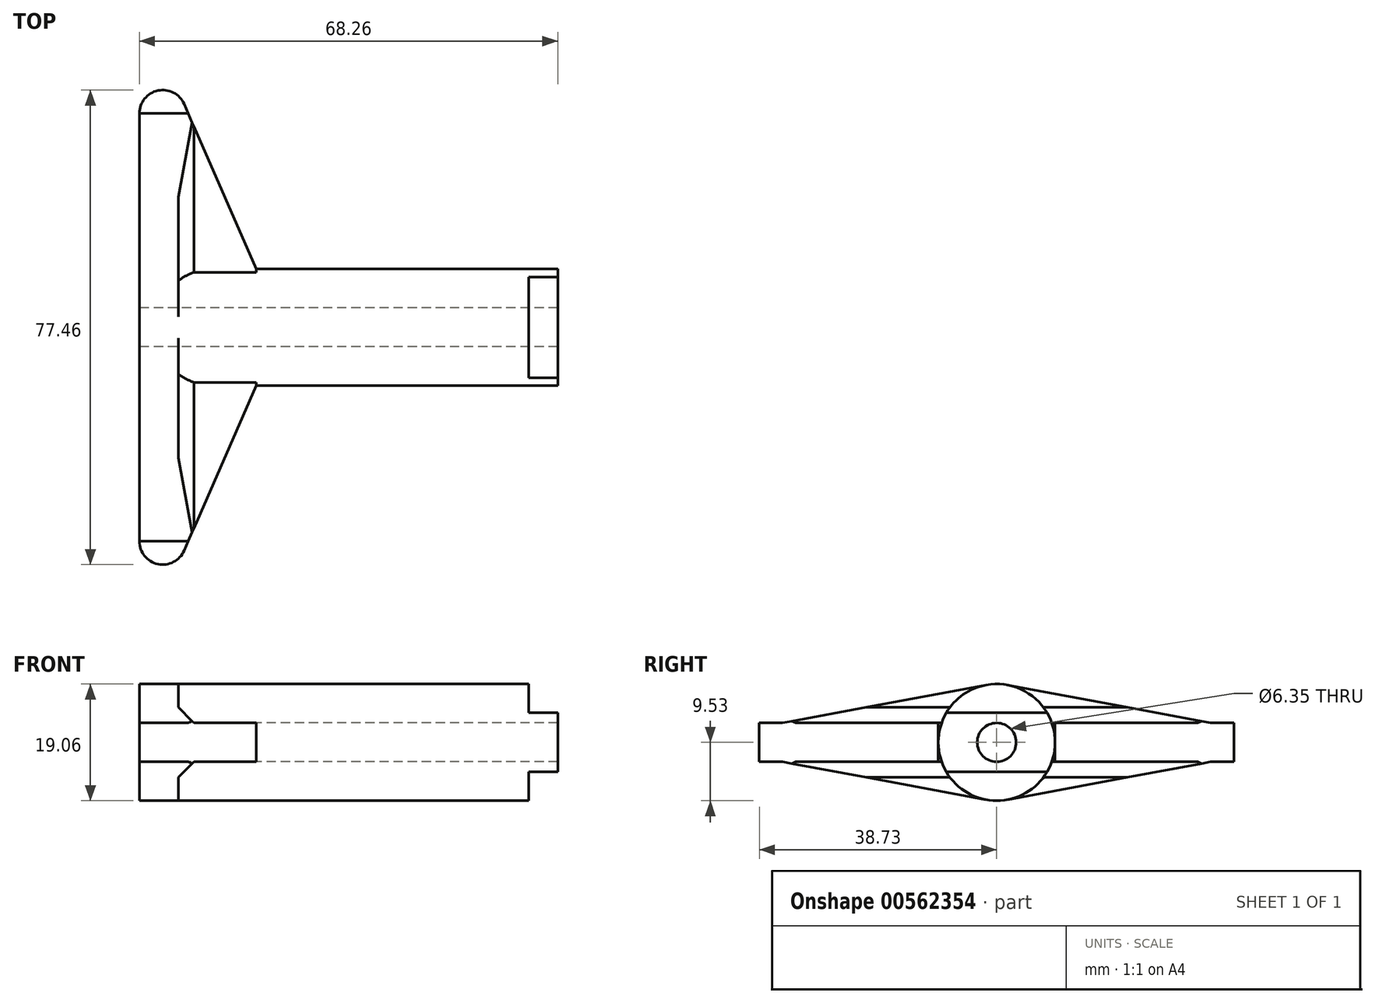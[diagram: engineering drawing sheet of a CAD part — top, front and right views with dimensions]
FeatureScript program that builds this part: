
annotation { "Feature Type Name" : "Feature", "Feature Type Description" : "" }
export const myFeature = defineFeature(function(context is Context, id is Id, definition is map)
    precondition{}
    {
        {
            var Q0;
            Q0=qCreatedBy(makeId("Right.planeOp"),FACE);
            var sketch = newSketch(context, id + "F0", { "sketchPlane" : qUnion([Q0])});
            skCircle(sketch, "E0", {"center": v(0, 0) * mm, "radius": 9.53 * mm});
            skCircle(sketch, "E1", {"center": v(0, 0) * mm, "radius": 3.18 * mm});
            skLineSegment(sketch, "E2", {"start": v(-15.88, 4.83) * mm, "end": v(24.18, 4.83) * mm});
            skLineSegment(sketch, "E3", {"start": v(26.07, -4.83) * mm, "end": v(-16.45, -4.83) * mm});
            skSolve(sketch);
        }
        {
            var Q0;
            Q0=makeQuery(id+"F0.imprint","IMPRINT",FACE,{"disambiguationData":[TD([[makeQuery(id+"F0.imprint","IMPRINT",EDGE,{"derivedFrom":sQuery(id+"F0.wireOp",EDGE,"E1")}),-1.0]])]});
            extrude(context, id + "F1", {"entities" : qUnion([Q0]), "depth" : 4.76 * mm, "offsetDistance" : 25.4 * mm});
        }
        {
            var Q0;
            Q0=makeQuery(id+"F1.opExtrude","CAP_FACE",FACE,{"disambiguationData":[OSD([sQuery(id+"F0.wireOp",EDGE,"E0"),sQuery(id+"F0.wireOp",EDGE,"E1"),sQuery(id+"F0.wireOp",EDGE,"E2"),sQuery(id+"F0.wireOp",EDGE,"E3")])],"isStart":true});
            var sketch = newSketch(context, id + "F2", { "sketchPlane" : qUnion([Q0])});
            skArc(sketch, "E4.0", {"start": v(-8.21, -4.83) * mm, "mid": v(-9.53, 0) * mm, "end": v(-8.21, 4.83) * mm});
            skCircle(sketch, "E5.0", {"center": v(0, 0) * mm, "radius": 3.18 * mm});
            skCircle(sketch, "E6", {"center": v(0, 0) * mm, "radius": 9.53 * mm});
            skSolve(sketch);
        }
        {
            var Q0;
            Q0 = qSketchRegion(id + "F2", true);
            extrude(context, id + "F3", {"entities" : qUnion([Q0]), "operationType" : NewBodyOperationType.ADD, "depth" : 63.5 * mm, "offsetDistance" : 25.4 * mm});
        }
        {
            var Q0;
            Q0=qCreatedBy(makeId("Top.planeOp"),FACE);
            var sketch = newSketch(context, id + "F4", { "sketchPlane" : qUnion([Q0])});
            skLineSegment(sketch, "E7.0", {"start": v(-63.5, -9.53) * mm, "end": v(-63.5, 9.52) * mm});
            skLineSegment(sketch, "E8", {"start": v(-63.5, 9.52) * mm, "end": v(-63.5, 34.92) * mm});
            skArc(sketch, "E9", {"start": v(-56.2, 36.45) * mm, "mid": v(-60.47, 38.65) * mm, "end": v(-63.5, 34.92) * mm});
            skLineSegment(sketch, "E10", {"start": v(-56.2, 36.45) * mm, "end": v(-44.45, 9.52) * mm});
            skLineSegment(sketch, "E11", {"start": v(-44.45, 9.52) * mm, "end": v(-44.45, -9.53) * mm});
            skLineSegment(sketch, "E12", {"start": v(-44.45, -9.52) * mm, "end": v(-56.2, -36.45) * mm});
            skArc(sketch, "E13", {"start": v(-63.5, -34.93) * mm, "mid": v(-60.47, -38.65) * mm, "end": v(-56.2, -36.45) * mm});
            skLineSegment(sketch, "E14", {"start": v(-63.5, -34.93) * mm, "end": v(-63.5, -9.53) * mm});
            skLineSegment(sketch, "E15", {"start": v(-63.5, -9.52) * mm, "end": v(-44.45, -9.52) * mm});
            skLineSegment(sketch, "E16", {"start": v(-63.5, 9.53) * mm, "end": v(-44.45, 9.53) * mm});
            skSolve(sketch);
        }
        {
            var Q0;
            Q0 = qSketchRegion(id + "F4", true);
            extrude(context, id + "F5", {"entities" : qUnion([Q0]), "operationType" : NewBodyOperationType.ADD, "endBound" : BoundingType.SYMMETRIC, "depth" : 6.35 * mm, "offsetDistance" : 25.4 * mm});
        }
        {
            var Q0;
            Q0=makeQuery(id+"F5.boolean.opBoolean","MERGE",FACE,{"derivedFrom":[makeQuery(id+"F3.opExtrude","CAP_FACE",FACE,{"disambiguationData":[OSD([sQuery(id+"F2.wireOp",EDGE,"E5.0"),sQuery(id+"F2.wireOp",EDGE,"E6")])],"isStart":false}),makeQuery(id+"F5.opExtrude","SWEPT_FACE",FACE,{"disambiguationData":[OSD([sQuery(id+"F4.wireOp",EDGE,"E7.0"),sQuery(id+"F4.wireOp",EDGE,"E8"),sQuery(id+"F4.wireOp",EDGE,"E14")])]})]});
            var sketch = newSketch(context, id + "F6", { "sketchPlane" : qUnion([Q0])});
            skLineSegment(sketch, "E17", {"start": v(-34.92, 3.18) * mm, "end": v(0, 9.69) * mm});
            skPoint(sketch, "E17.endSnap0", {"position": v(0, 9.53) * mm});
            skLineSegment(sketch, "E18", {"start": v(0, 9.69) * mm, "end": v(34.93, 3.18) * mm});
            skLineSegment(sketch, "E19", {"start": v(34.93, 3.18) * mm, "end": v(34.93, -3.18) * mm});
            skLineSegment(sketch, "E20", {"start": v(34.93, -3.17) * mm, "end": v(0, -9.69) * mm});
            skLineSegment(sketch, "E21", {"start": v(0, -9.69) * mm, "end": v(-34.92, -3.18) * mm});
            skLineSegment(sketch, "E22", {"start": v(-34.92, -3.17) * mm, "end": v(-34.92, 3.17) * mm});
            skSolve(sketch);
        }
        {
            var Q0;
            Q0 = qSketchRegion(id + "F6", true);
            var Q1;
            {var subQ0=sQuery(id+"F6.wireOp",EDGE,"E21");Q1=makeQuery(id+"F6.imprint","IMPRINT",FACE,{"disambiguationData":[TD([[makeQuery(id+"F6.imprint","IMPRINT",EDGE,{"derivedFrom":subQ0}),-1.0]])]});}
            var Q2;
            {var subQ9=sQuery(id+"F4.wireOp",EDGE,"E14");var subQ10=sQuery(id+"F4.wireOp",EDGE,"E9");var subQ11=sQuery(id+"F4.wireOp",EDGE,"E8");var subQ12=sQuery(id+"F4.wireOp",EDGE,"E7.0");var subQ15=makeQuery(id+"F5.boolean.opBoolean","SPLIT",EDGE,{"disambiguationData":[TD([makeQuery(id+"F5.opExtrude","SWEPT_FACE",FACE,{"disambiguationData":[OSD([subQ10])]})])],"derivedFrom":makeQuery(id+"F5.opExtrude","CAP_EDGE",EDGE,{"disambiguationData":[OSD([subQ12,subQ11,subQ9])],"isStart":false})});Q2=makeQuery(id+"F6.imprint","IMPRINT",FACE,{"disambiguationData":[TD([[makeQuery(id+"F6.imprint","IMPRINT",EDGE,{"derivedFrom":subQ15}),-1.0]])]});}
            var Q3;
            {var subQ0=sQuery(id+"F6.wireOp",EDGE,"E18");Q3=makeQuery(id+"F6.imprint","IMPRINT",FACE,{"disambiguationData":[TD([[makeQuery(id+"F6.imprint","IMPRINT",EDGE,{"derivedFrom":subQ0}),-1.0]])]});}
            var Q4;
            {var subQ9=sQuery(id+"F4.wireOp",EDGE,"E14");var subQ10=sQuery(id+"F4.wireOp",EDGE,"E13");var subQ11=sQuery(id+"F4.wireOp",EDGE,"E8");var subQ12=sQuery(id+"F4.wireOp",EDGE,"E7.0");var subQ15=makeQuery(id+"F5.boolean.opBoolean","SPLIT",EDGE,{"disambiguationData":[TD([makeQuery(id+"F5.opExtrude","SWEPT_FACE",FACE,{"disambiguationData":[OSD([subQ10])]})])],"derivedFrom":makeQuery(id+"F5.opExtrude","CAP_EDGE",EDGE,{"disambiguationData":[OSD([subQ12,subQ11,subQ9])],"isStart":true})});Q4=makeQuery(id+"F6.imprint","IMPRINT",FACE,{"disambiguationData":[TD([[makeQuery(id+"F6.imprint","IMPRINT",EDGE,{"derivedFrom":subQ15}),1.0]])]});}
            var Q5;
            Q5=makeQuery(id+"F6.imprint","IMPRINT",FACE,{"disambiguationData":[TD([[makeQuery(id+"F6.imprint","IMPRINT",EDGE,{"derivedFrom":sQuery(id+"F6.wireOp",EDGE,"E19")}),-1.0]])]});
            extrude(context, id + "F7", {"entities" : qUnion([Q0, Q1, Q2, Q3, Q4, Q5]), "operationType" : NewBodyOperationType.ADD, "oppositeDirection" : true, "depth" : 6.35 * mm, "offsetDistance" : 25.4 * mm});
        }
        {
            var Q0;
            {var subQ0=sQuery(id+"F2.wireOp",EDGE,"E6");var subQ4=sQuery(id+"F4.wireOp",EDGE,"E11");var subQ5=sQuery(id+"F4.wireOp",EDGE,"E14");var subQ6=sQuery(id+"F4.wireOp",EDGE,"E8");var subQ7=sQuery(id+"F4.wireOp",EDGE,"E7.0");var subQ8=sQuery(id+"F4.wireOp",EDGE,"E9");var subQ9=sQuery(id+"F4.wireOp",EDGE,"E10");Q0=makeQuery(id+"F7.boolean.opBoolean","INTERSECT",EDGE,{"derivedFrom":[makeQuery(id+"F5.boolean.opBoolean","SPLIT",FACE,{"disambiguationData":[TD([makeQuery(id+"F5.opExtrude","SWEPT_FACE",FACE,{"disambiguationData":[OSD([subQ8])]})])],"derivedFrom":makeQuery(id+"F5.opExtrude","CAP_FACE",FACE,{"disambiguationData":[OSD([subQ7,subQ6,subQ8,subQ9,subQ4,sQuery(id+"F4.wireOp",EDGE,"E12"),sQuery(id+"F4.wireOp",EDGE,"E13"),subQ5])],"isStart":false})}),makeQuery(id+"F7.opExtrude","CAP_FACE",FACE,{"disambiguationData":[OSD([subQ0,sQuery(id+"F6.wireOp",EDGE,"E17"),sQuery(id+"F6.wireOp",EDGE,"E18"),sQuery(id+"F6.wireOp",EDGE,"E19"),sQuery(id+"F6.wireOp",EDGE,"E20"),sQuery(id+"F6.wireOp",EDGE,"E21"),sQuery(id+"F6.wireOp",EDGE,"E22")])],"isStart":false})]});}
            var Q1;
            {var subQ0=sQuery(id+"F2.wireOp",EDGE,"E6");var subQ4=sQuery(id+"F4.wireOp",EDGE,"E11");var subQ5=sQuery(id+"F4.wireOp",EDGE,"E14");var subQ6=sQuery(id+"F4.wireOp",EDGE,"E8");var subQ7=sQuery(id+"F4.wireOp",EDGE,"E7.0");var subQ8=sQuery(id+"F4.wireOp",EDGE,"E9");var subQ9=sQuery(id+"F4.wireOp",EDGE,"E10");Q1=makeQuery(id+"F7.boolean.opBoolean","INTERSECT",EDGE,{"derivedFrom":[makeQuery(id+"F5.boolean.opBoolean","SPLIT",FACE,{"disambiguationData":[TD([makeQuery(id+"F5.opExtrude","SWEPT_FACE",FACE,{"disambiguationData":[OSD([subQ8])]})])],"derivedFrom":makeQuery(id+"F5.opExtrude","CAP_FACE",FACE,{"disambiguationData":[OSD([subQ7,subQ6,subQ8,subQ9,subQ4,sQuery(id+"F4.wireOp",EDGE,"E12"),sQuery(id+"F4.wireOp",EDGE,"E13"),subQ5])],"isStart":true})}),makeQuery(id+"F7.opExtrude","CAP_FACE",FACE,{"disambiguationData":[OSD([subQ0,sQuery(id+"F6.wireOp",EDGE,"E17"),sQuery(id+"F6.wireOp",EDGE,"E18"),sQuery(id+"F6.wireOp",EDGE,"E19"),sQuery(id+"F6.wireOp",EDGE,"E20"),sQuery(id+"F6.wireOp",EDGE,"E21"),sQuery(id+"F6.wireOp",EDGE,"E22")])],"isStart":false})]});}
            var Q2;
            {var subQ0=sQuery(id+"F2.wireOp",EDGE,"E6");var subQ4=sQuery(id+"F4.wireOp",EDGE,"E11");var subQ5=sQuery(id+"F4.wireOp",EDGE,"E14");var subQ6=sQuery(id+"F4.wireOp",EDGE,"E8");var subQ7=sQuery(id+"F4.wireOp",EDGE,"E7.0");var subQ8=sQuery(id+"F4.wireOp",EDGE,"E12");var subQ9=sQuery(id+"F4.wireOp",EDGE,"E13");Q2=makeQuery(id+"F7.boolean.opBoolean","INTERSECT",EDGE,{"derivedFrom":[makeQuery(id+"F5.boolean.opBoolean","SPLIT",FACE,{"disambiguationData":[TD([makeQuery(id+"F5.opExtrude","SWEPT_FACE",FACE,{"disambiguationData":[OSD([subQ8])]})])],"derivedFrom":makeQuery(id+"F5.opExtrude","CAP_FACE",FACE,{"disambiguationData":[OSD([subQ7,subQ6,sQuery(id+"F4.wireOp",EDGE,"E9"),sQuery(id+"F4.wireOp",EDGE,"E10"),subQ4,subQ8,subQ9,subQ5])],"isStart":false})}),makeQuery(id+"F7.opExtrude","CAP_FACE",FACE,{"disambiguationData":[OSD([subQ0,sQuery(id+"F6.wireOp",EDGE,"E17"),sQuery(id+"F6.wireOp",EDGE,"E18"),sQuery(id+"F6.wireOp",EDGE,"E19"),sQuery(id+"F6.wireOp",EDGE,"E20"),sQuery(id+"F6.wireOp",EDGE,"E21"),sQuery(id+"F6.wireOp",EDGE,"E22")])],"isStart":false})]});}
            var Q3;
            {var subQ0=sQuery(id+"F2.wireOp",EDGE,"E6");var subQ4=sQuery(id+"F4.wireOp",EDGE,"E11");var subQ5=sQuery(id+"F4.wireOp",EDGE,"E14");var subQ6=sQuery(id+"F4.wireOp",EDGE,"E8");var subQ7=sQuery(id+"F4.wireOp",EDGE,"E7.0");var subQ8=sQuery(id+"F4.wireOp",EDGE,"E12");var subQ9=sQuery(id+"F4.wireOp",EDGE,"E13");Q3=makeQuery(id+"F7.boolean.opBoolean","INTERSECT",EDGE,{"derivedFrom":[makeQuery(id+"F5.boolean.opBoolean","SPLIT",FACE,{"disambiguationData":[TD([makeQuery(id+"F5.opExtrude","SWEPT_FACE",FACE,{"disambiguationData":[OSD([subQ8])]})])],"derivedFrom":makeQuery(id+"F5.opExtrude","CAP_FACE",FACE,{"disambiguationData":[OSD([subQ7,subQ6,sQuery(id+"F4.wireOp",EDGE,"E9"),sQuery(id+"F4.wireOp",EDGE,"E10"),subQ4,subQ8,subQ9,subQ5])],"isStart":true})}),makeQuery(id+"F7.opExtrude","CAP_FACE",FACE,{"disambiguationData":[OSD([subQ0,sQuery(id+"F6.wireOp",EDGE,"E17"),sQuery(id+"F6.wireOp",EDGE,"E18"),sQuery(id+"F6.wireOp",EDGE,"E19"),sQuery(id+"F6.wireOp",EDGE,"E20"),sQuery(id+"F6.wireOp",EDGE,"E21"),sQuery(id+"F6.wireOp",EDGE,"E22")])],"isStart":false})]});}
            chamfer(context, id + "F8", {"entities" : qUnion([Q0, Q1, Q2, Q3]), "width" : 2.54 * mm, "tangentPropagation" : true});
        }
        {
            var Q0;
            Q0=makeQuery(id+"F1.opExtrude","CAP_FACE",FACE,{"disambiguationData":[OSD([sQuery(id+"F0.wireOp",EDGE,"E0"),sQuery(id+"F0.wireOp",EDGE,"E1"),sQuery(id+"F0.wireOp",EDGE,"E2"),sQuery(id+"F0.wireOp",EDGE,"E3")])],"isStart":false});
            var sketch = newSketch(context, id + "F9", { "sketchPlane" : qUnion([Q0])});
            skCircle(sketch, "E23.0", {"center": v(0, 0) * mm, "radius": 3.18 * mm});
            skSolve(sketch);
        }
        {
            var Q0;
            Q0 = qSketchRegion(id + "F9", true);
            extrude(context, id + "F10", {"entities" : qUnion([Q0]), "operationType" : NewBodyOperationType.REMOVE, "endBound" : BoundingType.THROUGH_ALL, "oppositeDirection" : true, "depth" : 25.4 * mm, "offsetDistance" : 25.4 * mm});
        }
    });
